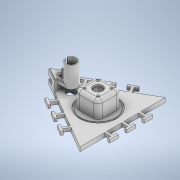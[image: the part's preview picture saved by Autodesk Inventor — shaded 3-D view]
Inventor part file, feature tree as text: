
AUTODESK INVENTOR PART (.ipt)
format: ipt  version: 2022.3 (Build 263350000, 350)  size: 585,216 bytes
history: native  units: mm
features: extrude x21, sketch x14, fillet x7, projected_geometry x2, hole x1
ambient origin geometry x8: Origin, YZ Plane, XZ Plane, XY Plane, X Axis, Y Axis, Z Axis, Center Point
bodies: Solid1 (feature_tree)
feature tree (45):
  sketch  "Sketch1"  dims[d0=200.0mm d1=35.0mm]
  extrude  "Extrusion1"  Depth=35.0mm
  extrude  "Extrusion2"  Depth=5.0mm
  sketch  "Sketch2"  dims[d2=5.0mm d3=5.0mm]
  extrude  "Extrusion3"  Depth=20.0mm
  extrude  "Extrusion4"  Depth=10.0mm TaperAngle=0.0deg
  extrude  "Extrusion5"  Depth=54.0mm
  hole  "Hole1"  [1 undecoded]
  fillet  "Fillet1"  Radius=22.0mm
  fillet  "Fillet2"  [1 undecoded]
  extrude  "Extrusion6"  Depth=35.0mm TaperAngle=0.0deg
  extrude  "Extrusion7"  Depth=31.0mm
  sketch  "Sketch6"  dims[d22=54.0mm d23=5.5mm d24=22.0mm d25=0.0mm d26=0.0mm]
  extrude  "Extrusion8"  Depth=10.0mm
  extrude  "Extrusion9"  Depth=8.0mm
  sketch  "Sketch7"  dims[d27=40.0mm d28=0.0mm d29=35.0mm d30=0.0mm]
  extrude  "Extrusion10"  Depth=2.8mm TaperAngle=0.0deg
  extrude  "Extrusion11"  Depth=3.0mm
  extrude  "Extrusion12"  Depth=1.5mm
  sketch  "Sketch8"  dims[d31=31.0mm d32=31.0mm]
  extrude  "Extrusion13"  Depth=4.0mm
  extrude  "Extrusion14"  Depth=18.0mm
  extrude  "Extrusion15"  Depth=20.0mm TaperAngle=0.0deg
  sketch  "Sketch10"  dims[d41=8.0mm d42=80.0mm]
  extrude  "Extrusion16"  Depth=20.0mm TaperAngle=0.0deg
  extrude  "Extrusion17"  Depth=63.0mm
  extrude  "Extrusion18"  Depth=4.0mm
  fillet  "Fillet3"  Radius=26.0mm
  fillet  "Fillet4"  Radius=8.2mm
  extrude  "Extrusion19"  Depth=4.0mm TaperAngle=0.0deg
  extrude  "Extrusion20"  Depth=15.0mm TaperAngle=0.0deg
  extrude  "Extrusion21"  Depth=20.0mm
  fillet  "Fillet5"  [1 undecoded]
  fillet  "Fillet6"  Radius=22.0mm
  fillet  "Fillet7"  Radius=6.0mm
  sketch  "Sketch3"  dims[d4=20.0mm d5=20.0mm d7=40.0mm d8=20.0mm d10=40.0mm]
  sketch  "Sketch4"  dims[d13=30.0mm d15=360.0deg d17=10.0mm d18=0.0mm]
  sketch  "Sketch5"  dims[d19=2.5mm d20=0.0mm d21=54.0mm]
  sketch  "Sketch9"  dims[d33=3.4mm d34=6.0mm d35=5.9mm d36=2.0mm d37=90.0deg d38=5.0mm d39=0.0mm d40=10.0mm]
  projected_geometry  "Projected Loop1"
  projected_geometry  "Projected Loop2"
  sketch  "Sketch11"  dims[d43=3.5mm d44=2.8mm d45=0.0mm]
  sketch  "Sketch12"  dims[d46=120.0mm d47=3.0mm]
  sketch  "Sketch13"  dims[d48=1.5mm d49=0.0mm d50=31.0mm]
  sketch  "Sketch14"  dims[d51=18.0mm d52=9.0mm d53=18.0mm d54=20.0mm d55=0.0mm d56=20.0mm d57=0.0mm d58=63.0mm d59=19.5mm d61=26.0mm d62=8.2mm d63=24.0mm d64=0.0mm d65=15.0mm d66=0.0mm d67=20.0mm d68=0.0mm d69=0.0mm d70=22.0mm d71=6.0mm d72=6.0mm d73=3.0mm d74=4.0mm d75=2.0mm d76=2.0mm d77=20.0mm d78=0.0mm d79=40.0mm d80=0.0mm d81=1.5mm d82=2.0mm d83=0.0mm d84=2.0mm d85=12.0mm d86=18.0mm d87=0.0mm d88=0.0mm d89=14.5mm d90=0.0mm d91=18.0mm d92=8.0mm d93=0.0mm d94=0.0mm d95=4.0mm d96=2.0mm d97=3.0mm d98=0.0mm d99=18.0mm d100=8.0mm d101=1.0mm d102=2.0mm d103=0.0mm d104=20.0mm d105=5.0mm d106=0.0mm d107=2.0mm d108=4.0mm d109=4.0mm d110=0.0mm d111=0.0mm d112=0.0mm]
note: 3 required parameter values undecoded (feature->parameter linkage not recoverable at this tier; creation-order binding heuristic only, values carry confidence <= 0.55)
